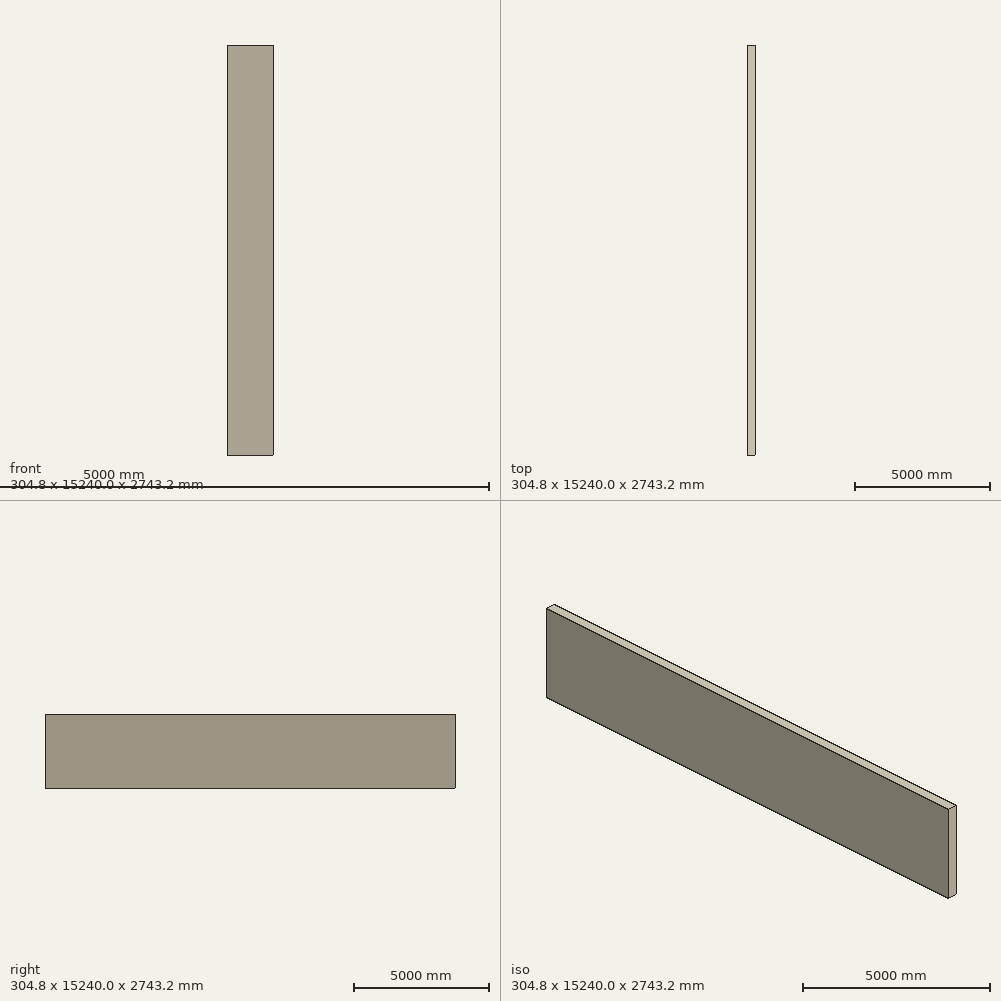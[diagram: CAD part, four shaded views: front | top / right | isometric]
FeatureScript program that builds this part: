
annotation { "Feature Type Name" : "Feature", "Feature Type Description" : "" }
export const myFeature = defineFeature(function(context is Context, id is Id, definition is map)
    precondition{}
    {
        {
            var Q0;
            Q0=qCreatedBy(makeId("Front.planeOp"),FACE);
            var sketch = newSketch(context, id + "F0", { "sketchPlane" : qUnion([Q0])});
            skLineSegment(sketch, "E0.bottom", {"start": v(-210.27, 1024.76) * mm, "end": v(94.53, 1024.76) * mm});
            skLineSegment(sketch, "E0.top", {"start": v(-210.27, -1718.44) * mm, "end": v(94.53, -1718.44) * mm});
            skLineSegment(sketch, "E0.left", {"start": v(-210.27, 1024.76) * mm, "end": v(-210.27, -1718.44) * mm});
            skLineSegment(sketch, "E0.right", {"start": v(94.53, 1024.76) * mm, "end": v(94.53, -1718.44) * mm});
            skSolve(sketch);
        }
        {
            var Q0;
            Q0 = qSketchRegion(id + "F0", true);
            extrude(context, id + "F1", {"entities" : qUnion([Q0]), "depth" : 15240 * mm, "offsetDistance" : 25.4 * mm});
        }
    });
